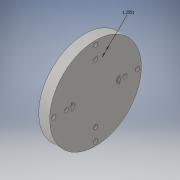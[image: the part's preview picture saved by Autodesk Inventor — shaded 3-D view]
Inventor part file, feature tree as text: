
AUTODESK INVENTOR PART (.ipt)
format: ipt  version: 2016 (Build 200138000, 138)  size: 188,416 bytes
history: native  units: in
note: dims shown in document units (in); Inventor stores cm internally (conversion verified against a paired STEP export)
features: sketch x7, extrude x3, revolve x1, hole x1
ambient origin geometry x8: Origin, YZ Plane, XZ Plane, XY Plane, X Axis, Y Axis, Z Axis, Center Point
bodies: Solid1 (feature_tree)
feature tree (12):
  revolve  "Revolution1"  [1 undecoded]
  extrude  "Extrusion1"  Depth=0.105in
  sketch  "Sketch3"  dims[d4=0.105in d5=0.255in]
  sketch  "Sketch4"  dims[d6=0.2in d7=0.1in]
  extrude  "Extrusion2"  Depth=0.105in
  sketch  "Sketch5"  dims[d8=90.0deg d9=0.1181in]
  extrude  "Extrusion3"  Depth=0.1in
  hole  "Hole1"  [1 undecoded]
  sketch  "Sketch1"  dims[d0=1.2499in d1=0.3in]
  sketch  "Sketch2"  dims[d2=0.22in d3=0.105in]
  sketch  "Sketch6"  dims[d10=1.5748in d12=360.0deg]
  sketch  "Sketch7"  dims[d14=0.5in d15=0.0in d16=0.255in d17=0.1275in d18=0.1181in d19=1.5748in d21=360.0deg d23=0.2in d24=0.0in d25=1.14in d26=0.787in d27=0.2in d28=0.2in d29=0.5in d30=0.0in d34=0.22in d35=0.144in d36=0.75in d37=0.375in d38=0.25in d39=0.5635in d40=0.05in d41=0.8108in]
note: 2 required parameter values undecoded (feature->parameter linkage not recoverable at this tier; creation-order binding heuristic only, values carry confidence <= 0.55)